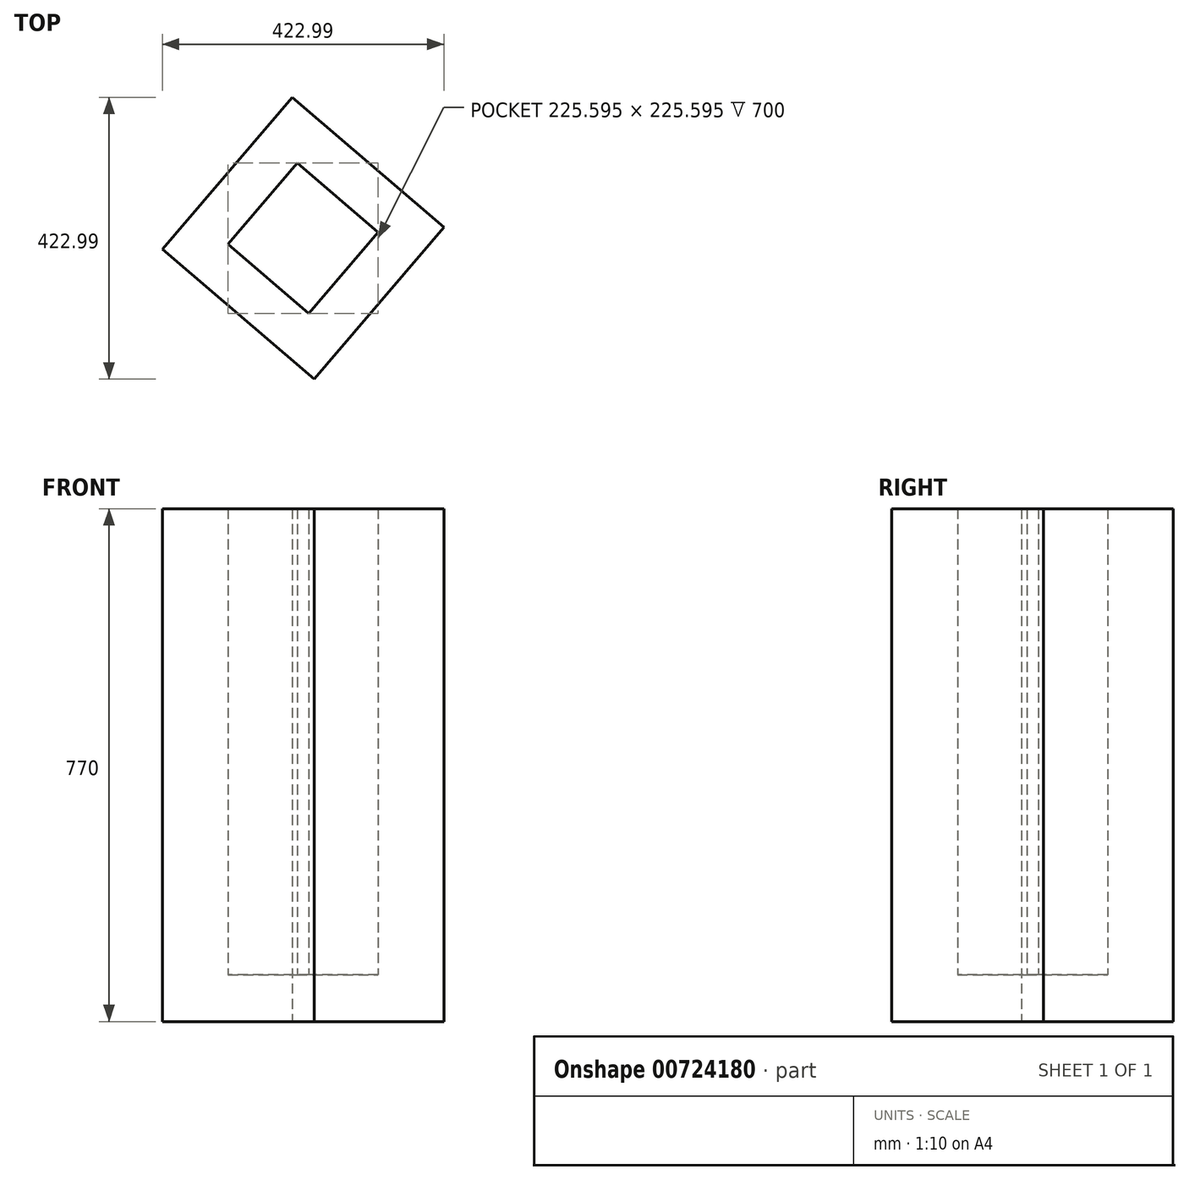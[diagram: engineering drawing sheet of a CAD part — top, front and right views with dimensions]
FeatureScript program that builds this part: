
annotation { "Feature Type Name" : "Feature", "Feature Type Description" : "" }
export const myFeature = defineFeature(function(context is Context, id is Id, definition is map)
    precondition{}
    {
        {
            var Q0;
            Q0=qCreatedBy(makeId("Top.planeOp"),FACE);
            var sketch = newSketch(context, id + "F0", { "sketchPlane" : qUnion([Q0])});
            skCircle(sketch, "E0.cCircle", {"center": v(-88.46, 73.4) * mm, "radius": 150 * mm, "construction": true});
            skLineSegment(sketch, "E0.0", {"start": v(123.04, 89.82) * mm, "end": v(-72.03, -138.1) * mm});
            skLineSegment(sketch, "E0.1", {"start": v(-72.03, -138.1) * mm, "end": v(-299.95, 56.97) * mm});
            skLineSegment(sketch, "E0.2", {"start": v(-299.95, 56.97) * mm, "end": v(-104.88, 284.89) * mm});
            skLineSegment(sketch, "E0.3", {"start": v(-104.88, 284.89) * mm, "end": v(123.04, 89.82) * mm});
            skPoint(sketch, "E0.0.midPoint", {"position": v(25.5, -24.14) * mm});
            skSolve(sketch);
        }
        {
            var Q0;
            Q0=makeQuery(id+"F0.imprint","IMPRINT",FACE,{"disambiguationData":[TD([[makeQuery(id+"F0.imprint","IMPRINT",EDGE,{"derivedFrom":sQuery(id+"F0.wireOp",EDGE,"E0.0")}),-1.0]])]});
            extrude(context, id + "F1", {"entities" : qUnion([Q0]), "depth" : 770 * mm, "offsetDistance" : 25 * mm});
        }
        {
            var Q0;
            Q0=makeQuery(id+"F1.opExtrude","CAP_FACE",FACE,{"disambiguationData":[OSD([sQuery(id+"F0.wireOp",EDGE,"E0.0"),sQuery(id+"F0.wireOp",EDGE,"E0.1"),sQuery(id+"F0.wireOp",EDGE,"E0.2"),sQuery(id+"F0.wireOp",EDGE,"E0.3")])],"isStart":false});
            shell(context, id + "F2", {"entities" : qUnion([Q0]), "thickness" : 70 * mm});
        }
    });
